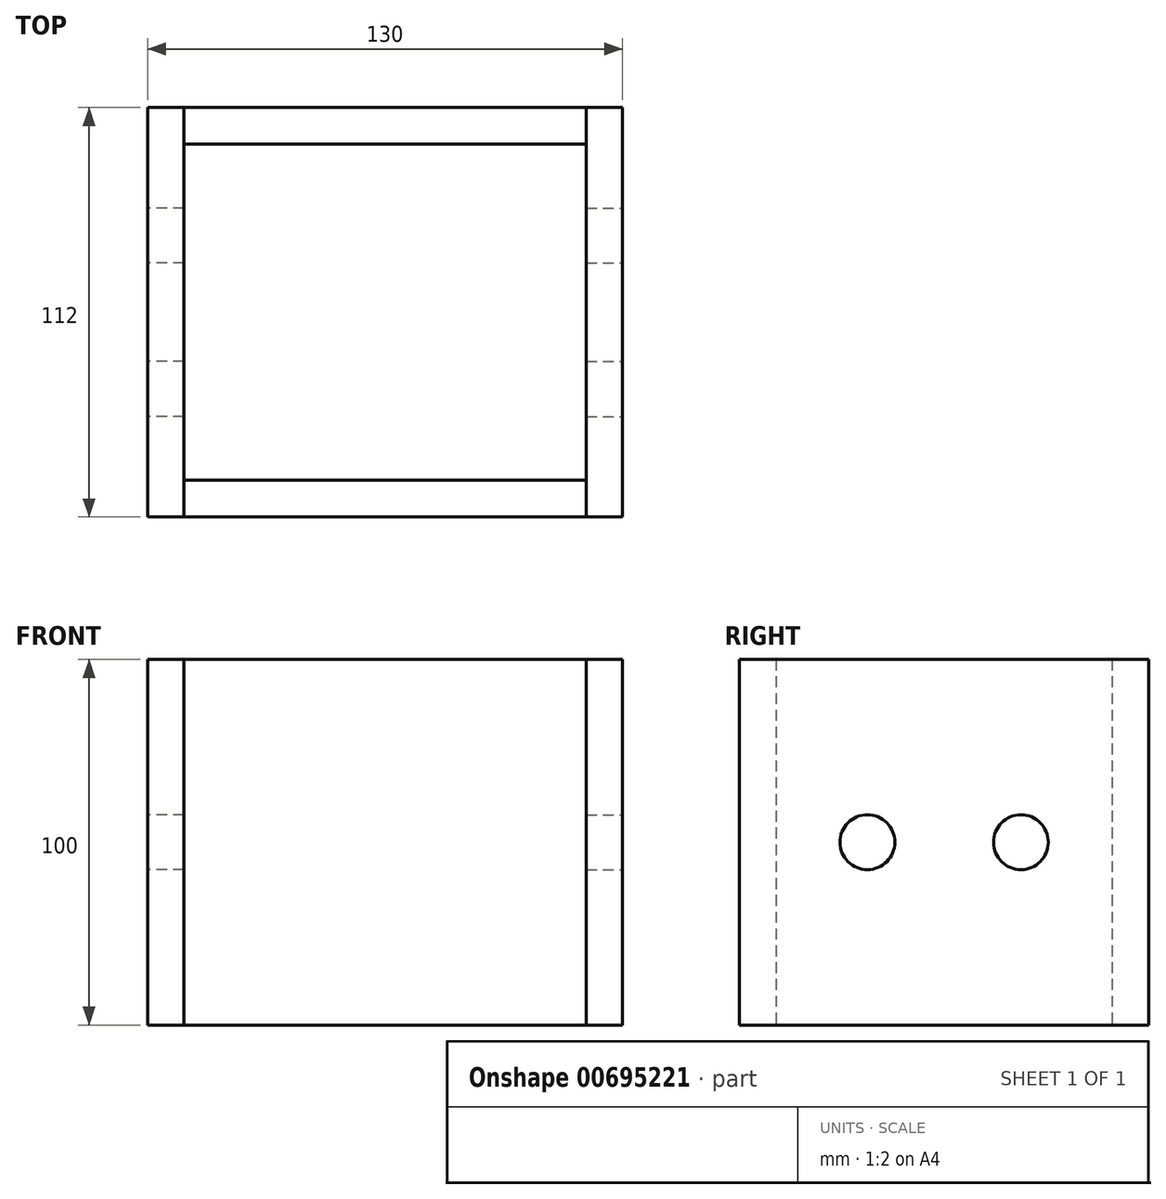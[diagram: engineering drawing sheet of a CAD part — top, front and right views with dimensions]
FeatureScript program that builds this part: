
annotation { "Feature Type Name" : "Feature", "Feature Type Description" : "" }
export const myFeature = defineFeature(function(context is Context, id is Id, definition is map)
    precondition{}
    {
        {
            var Q0;
            Q0=qCreatedBy(makeId("Right.planeOp"),FACE);
            var sketch = newSketch(context, id + "F0", { "sketchPlane" : qUnion([Q0])});
            skLineSegment(sketch, "E0.bottom", {"start": v(-35, 50) * mm, "end": v(21, 50) * mm});
            skLineSegment(sketch, "E0.top", {"start": v(-35, -50) * mm, "end": v(21, -50) * mm});
            skLineSegment(sketch, "E0.left", {"start": v(-35, 50) * mm, "end": v(-35, -50) * mm});
            skLineSegment(sketch, "E0.right", {"start": v(21, 50) * mm, "end": v(21, -50) * mm});
            skCircle(sketch, "E1", {"center": v(0, 0) * mm, "radius": 7.5 * mm});
            skSolve(sketch);
        }
        {
            var Q0;
            Q0=makeQuery(id+"F0.imprint","IMPRINT",FACE,{"disambiguationData":[TD([[makeQuery(id+"F0.imprint","IMPRINT",EDGE,{"derivedFrom":sQuery(id+"F0.wireOp",EDGE,"E0.bottom")}),-1.0]])]});
            extrude(context, id + "F1", {"entities" : qUnion([Q0]), "depth" : 10 * mm});
        }
        {
            var Q0;
            Q0=makeQuery(id+"F1.opExtrude","SWEPT_BODY",BODY,{"disambiguationData":[OSD([sQuery(id+"F0.wireOp",EDGE,"E0.bottom"),sQuery(id+"F0.wireOp",EDGE,"E0.top"),sQuery(id+"F0.wireOp",EDGE,"E0.left"),sQuery(id+"F0.wireOp",EDGE,"E0.right"),sQuery(id+"F0.wireOp",EDGE,"rgaBh7ed-yzeX-51PE-KJwg-0XFkLaL4d9ET"),sQuery(id+"F0.wireOp",EDGE,"PRCWQJZA-zwb4-kcCU-vDn6-fWhEnT45CPGa"),sQuery(id+"F0.wireOp",EDGE,"24f5492e-8ac3-413e-9412-904b776a6be8.trimOffspring"),sQuery(id+"F0.wireOp",EDGE,"954fe64b-5e16-4ffe-b02d-878927013ef90.MirrorCS")])]});
            var Q1;
            Q1=makeQuery(id+"F1.opExtrude","SWEPT_FACE",FACE,{"disambiguationData":[OSD([sQuery(id+"F0.wireOp",EDGE,"E0.right")])]});
            mirror(context, id + "F2", {"operationType" : NewBodyOperationType.ADD, "entities" : qUnion([Q0]), "mirrorPlane" : qUnion([Q1])});
        }
        {
            var Q0;
            {var subQ0=makeQuery(id+"F1.opExtrude","CAP_FACE",FACE,{"disambiguationData":[OSD([sQuery(id+"F0.wireOp",EDGE,"E0.bottom"),sQuery(id+"F0.wireOp",EDGE,"E0.top"),sQuery(id+"F0.wireOp",EDGE,"E0.left"),sQuery(id+"F0.wireOp",EDGE,"E0.right"),sQuery(id+"F0.wireOp",EDGE,"rgaBh7ed-yzeX-51PE-KJwg-0XFkLaL4d9ET"),sQuery(id+"F0.wireOp",EDGE,"PRCWQJZA-zwb4-kcCU-vDn6-fWhEnT45CPGa"),sQuery(id+"F0.wireOp",EDGE,"24f5492e-8ac3-413e-9412-904b776a6be8.trimOffspring"),sQuery(id+"F0.wireOp",EDGE,"954fe64b-5e16-4ffe-b02d-878927013ef90.MirrorCS")])],"isStart":false});Q0=makeQuery(id+"F2.boolean.opBoolean","MERGE",FACE,{"derivedFrom":[subQ0,makeQuery(id+"F2.opPattern","COPY",FACE,{"derivedFrom":subQ0,"instanceName":"1"})]});}
            var sketch = newSketch(context, id + "F3", { "sketchPlane" : qUnion([Q0])});
            skLineSegment(sketch, "E2.0", {"start": v(-35, 50) * mm, "end": v(-35, -50) * mm});
            skLineSegment(sketch, "E3.0", {"start": v(-35, 50) * mm, "end": v(21, 50) * mm});
            skLineSegment(sketch, "E4.0", {"start": v(-35, -50) * mm, "end": v(21, -50) * mm});
            skLineSegment(sketch, "E5", {"start": v(-25, 50) * mm, "end": v(-25, -50) * mm});
            skSolve(sketch);
        }
        {
            var Q0;
            Q0=qSketchRegion(id+"F3",true);
            extrude(context, id + "F4", {"entities" : qUnion([Q0]), "depth" : 110 * mm});
        }
        {
            var Q0;
            Q0=makeQuery(id+"F2.opPattern","COPY",FACE,{"derivedFrom":makeQuery(id+"F1.opExtrude","SWEPT_FACE",FACE,{"disambiguationData":[OSD([sQuery(id+"F0.wireOp",EDGE,"E0.left")])]}),"instanceName":"1"});
            var Q1;
            Q1=makeQuery(id+"F1.opExtrude","SWEPT_FACE",FACE,{"disambiguationData":[OSD([sQuery(id+"F0.wireOp",EDGE,"E0.left")])]});
            cPlane(context, id + "F5", {"entities" : qUnion([Q0, Q1]), "cplaneType" : CPlaneType.MID_PLANE, "offset" : 25 * mm, "width" : 150 * mm, "height" : 150 * mm});
        }
        {
            var Q0;
            Q0=makeQuery(id+"F4.opExtrude","SWEPT_BODY",BODY,{"disambiguationData":[OSD([sQuery(id+"F3.wireOp",EDGE,"E2.0"),sQuery(id+"F3.wireOp",EDGE,"E3.0"),sQuery(id+"F3.wireOp",EDGE,"E4.0"),sQuery(id+"F3.wireOp",EDGE,"E5")])]});
            var Q1;
            Q1=qCreatedBy(id+"F5.planeOp",FACE);
            mirror(context, id + "F6", {"entities" : qUnion([Q0]), "mirrorPlane" : qUnion([Q1])});
        }
        {
            var Q0;
            {var subQ0=makeQuery(id+"F1.opExtrude","CAP_FACE",FACE,{"disambiguationData":[OSD([sQuery(id+"F0.wireOp",EDGE,"E0.bottom"),sQuery(id+"F0.wireOp",EDGE,"E0.top"),sQuery(id+"F0.wireOp",EDGE,"E0.left"),sQuery(id+"F0.wireOp",EDGE,"E0.right"),sQuery(id+"F0.wireOp",EDGE,"rgaBh7ed-yzeX-51PE-KJwg-0XFkLaL4d9ET"),sQuery(id+"F0.wireOp",EDGE,"PRCWQJZA-zwb4-kcCU-vDn6-fWhEnT45CPGa"),sQuery(id+"F0.wireOp",EDGE,"24f5492e-8ac3-413e-9412-904b776a6be8.trimOffspring"),sQuery(id+"F0.wireOp",EDGE,"954fe64b-5e16-4ffe-b02d-878927013ef90.MirrorCS")])],"isStart":false});Q0=makeQuery(id+"F2.boolean.opBoolean","MERGE",FACE,{"derivedFrom":[subQ0,makeQuery(id+"F2.opPattern","COPY",FACE,{"derivedFrom":subQ0,"instanceName":"1"})]});}
            var Q1;
            Q1=makeQuery(id+"F4.opExtrude","CAP_FACE",FACE,{"disambiguationData":[OSD([sQuery(id+"F3.wireOp",EDGE,"E2.0"),sQuery(id+"F3.wireOp",EDGE,"E3.0"),sQuery(id+"F3.wireOp",EDGE,"E4.0"),sQuery(id+"F3.wireOp",EDGE,"E5")])],"isStart":false});
            cPlane(context, id + "F7", {"entities" : qUnion([Q0, Q1]), "cplaneType" : CPlaneType.MID_PLANE, "offset" : 25 * mm, "width" : 150 * mm, "height" : 150 * mm});
        }
        {
            var Q0;
            Q0=makeQuery(id+"F1.opExtrude","SWEPT_BODY",BODY,{"disambiguationData":[OSD([sQuery(id+"F0.wireOp",EDGE,"E0.bottom"),sQuery(id+"F0.wireOp",EDGE,"E0.top"),sQuery(id+"F0.wireOp",EDGE,"E0.left"),sQuery(id+"F0.wireOp",EDGE,"E0.right"),sQuery(id+"F0.wireOp",EDGE,"rgaBh7ed-yzeX-51PE-KJwg-0XFkLaL4d9ET"),sQuery(id+"F0.wireOp",EDGE,"PRCWQJZA-zwb4-kcCU-vDn6-fWhEnT45CPGa"),sQuery(id+"F0.wireOp",EDGE,"24f5492e-8ac3-413e-9412-904b776a6be8.trimOffspring"),sQuery(id+"F0.wireOp",EDGE,"954fe64b-5e16-4ffe-b02d-878927013ef90.MirrorCS")])]});
            var Q1;
            Q1=qCreatedBy(id+"F7.planeOp",FACE);
            mirror(context, id + "F8", {"entities" : qUnion([Q0]), "mirrorPlane" : qUnion([Q1])});
        }
    });
